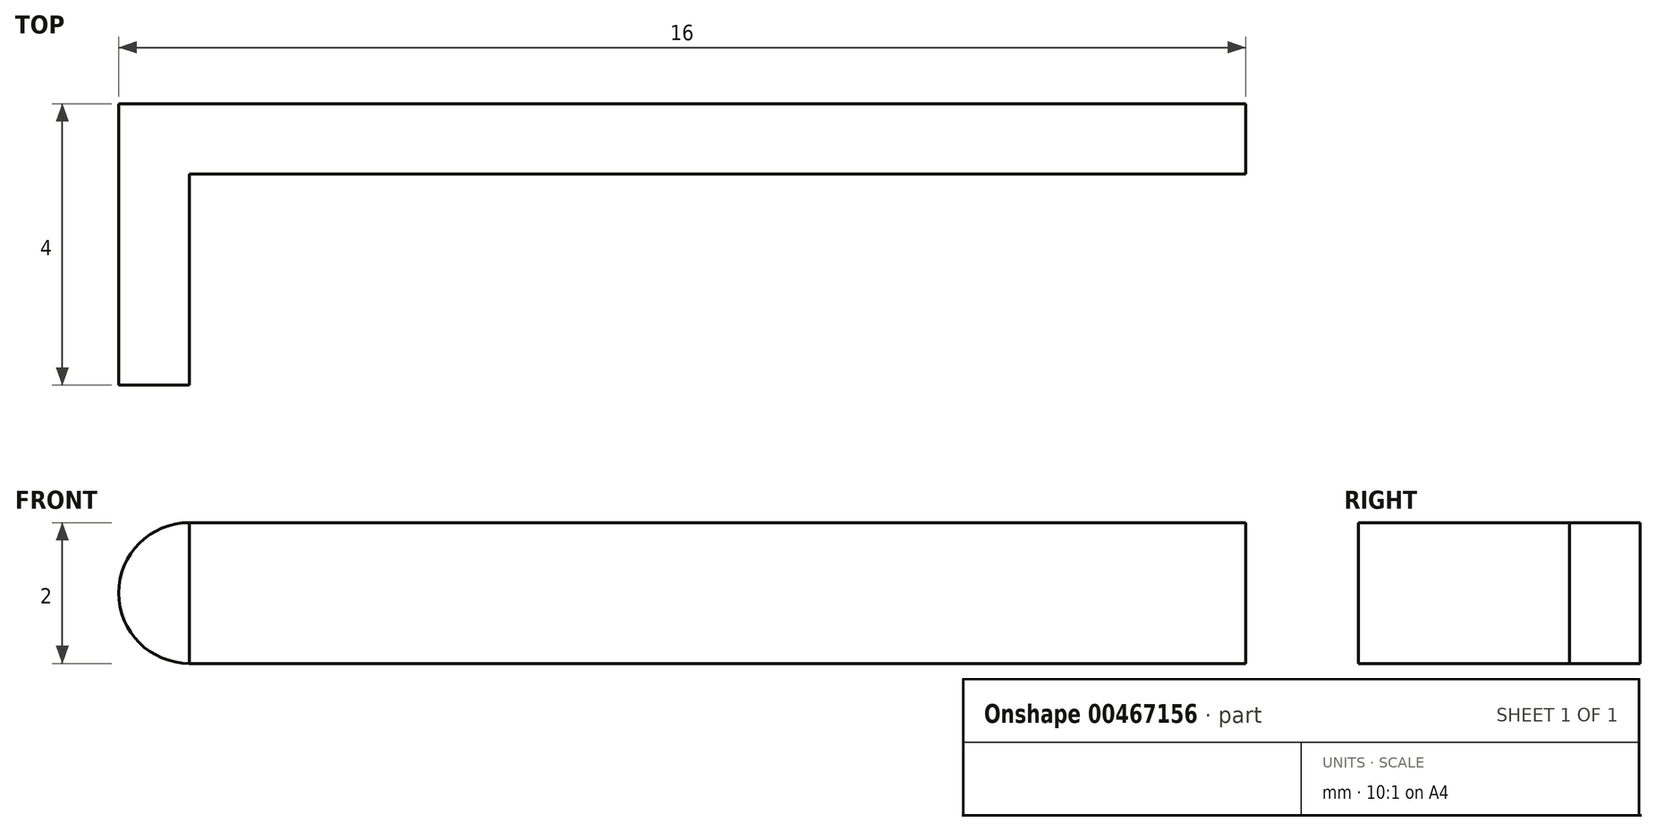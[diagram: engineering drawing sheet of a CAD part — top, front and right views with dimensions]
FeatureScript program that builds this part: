
annotation { "Feature Type Name" : "Feature", "Feature Type Description" : "" }
export const myFeature = defineFeature(function(context is Context, id is Id, definition is map)
    precondition{}
    {
        {
            assignVariable(context, id + "F0", {"name" : "SlideArmDepth", "anyValue" : 1});
        }
        {
            assignVariable(context, id + "F1", {"name" : "SlideHeadDepth", "anyValue" : (getVariable(context, 'SlideArmDepth') + 3)});
        }
        {
            var Q0;
            Q0=qCreatedBy(makeId("Front.planeOp"),FACE);
            var sketch = newSketch(context, id + "F2", { "sketchPlane" : qUnion([Q0])});
            skLineSegment(sketch, "E0.bottom", {"start": v(0, 1) * mm, "end": v(15, 1) * mm});
            skLineSegment(sketch, "E0.top", {"start": v(0, -1) * mm, "end": v(15, -1) * mm});
            skLineSegment(sketch, "E0.left", {"start": v(0, 1) * mm, "end": v(0, -1) * mm});
            skLineSegment(sketch, "E0.right", {"start": v(15, 1) * mm, "end": v(15, -1) * mm});
            skArc(sketch, "E1", {"start": v(0, 1) * mm, "mid": v(-1, 0) * mm, "end": v(0, -1) * mm});
            skSolve(sketch);
        }
        {
            var Q0;
            {var subQ0=sQuery(id+"F2.wireOp",EDGE,"E0.left");Q0=makeQuery(id+"F2.imprint","IMPRINT",FACE,{"disambiguationData":[TD([[makeQuery(id+"F2.imprint","IMPRINT",EDGE,{"derivedFrom":subQ0}),-1.0]])]});}
            extrude(context, id + "F3", {"entities" : qUnion([Q0]), "depth" : (getVariable(context, 'SlideHeadDepth')) * mm});
        }
        {
            var Q0;
            Q0=makeQuery(id+"F2.imprint","IMPRINT",FACE,{"disambiguationData":[TD([[makeQuery(id+"F2.imprint","IMPRINT",EDGE,{"derivedFrom":sQuery(id+"F2.wireOp",EDGE,"E0.bottom")}),-1.0]])]});
            extrude(context, id + "F4", {"entities" : qUnion([Q0]), "operationType" : NewBodyOperationType.ADD, "depth" : (getVariable(context, 'SlideArmDepth')) * mm});
        }
    });
